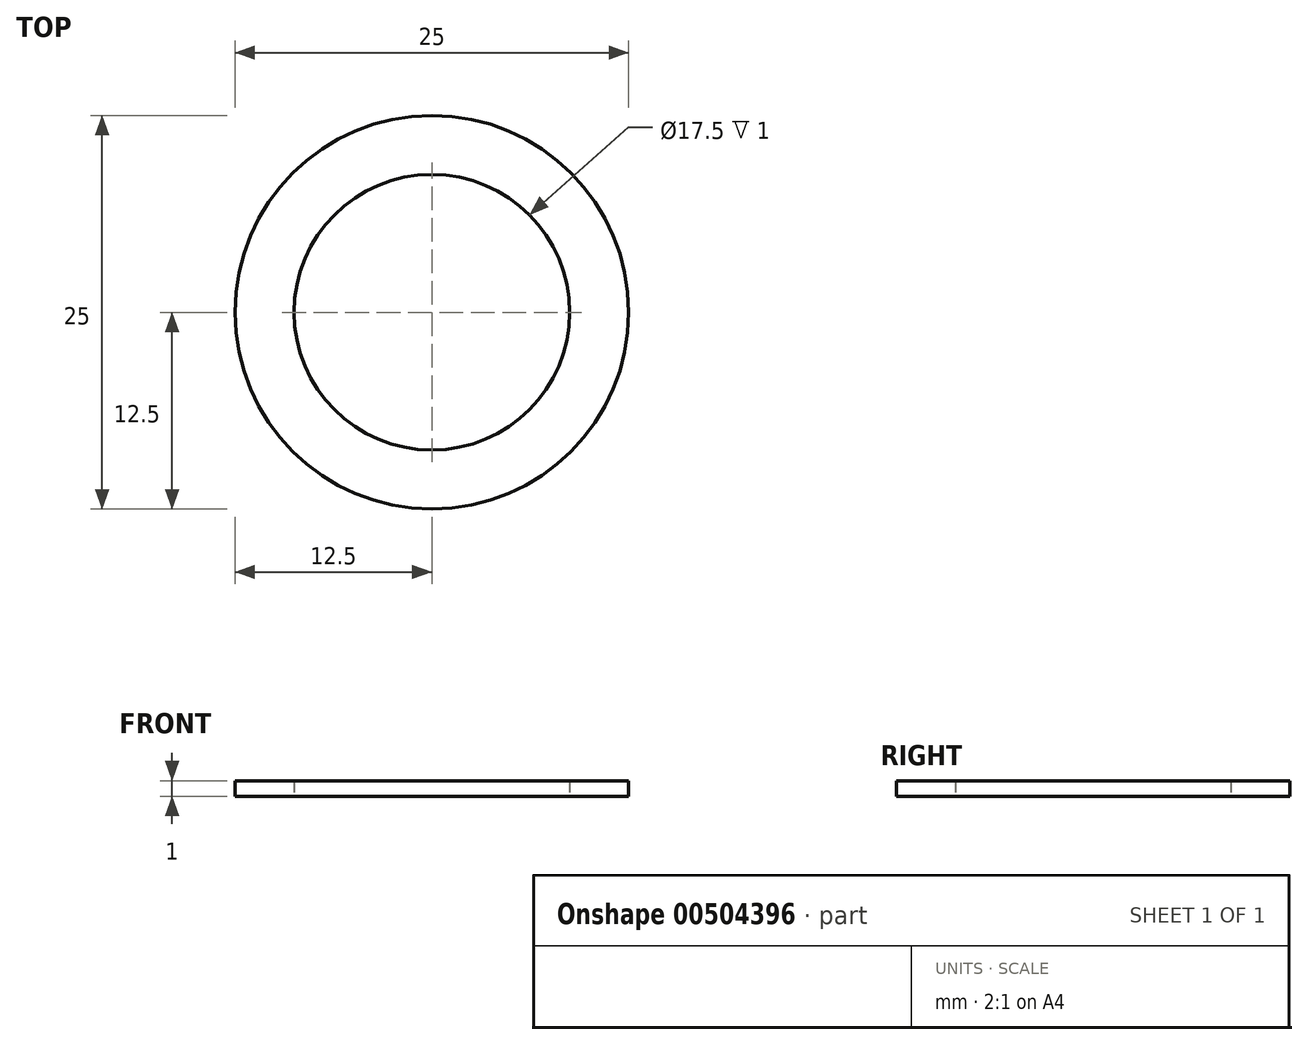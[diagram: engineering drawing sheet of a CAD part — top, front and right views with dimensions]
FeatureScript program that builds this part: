
annotation { "Feature Type Name" : "Feature", "Feature Type Description" : "" }
export const myFeature = defineFeature(function(context is Context, id is Id, definition is map)
    precondition{}
    {
        {
            var Q0;
            Q0=qCreatedBy(makeId("Top.planeOp"),FACE);
            var sketch = newSketch(context, id + "F0", { "sketchPlane" : qUnion([Q0])});
            skCircle(sketch, "E0", {"center": v(0, 0) * mm, "radius": 8.75 * mm});
            skCircle(sketch, "E1", {"center": v(0, 0) * mm, "radius": 12.5 * mm});
            skSolve(sketch);
        }
        {
            var Q0;
            Q0=makeQuery(id+"F0.imprint","IMPRINT",FACE,{"disambiguationData":[TD([[makeQuery(id+"F0.imprint","IMPRINT",EDGE,{"derivedFrom":sQuery(id+"F0.wireOp",EDGE,"E0")}),-1.0]])]});
            extrude(context, id + "F1", {"entities" : qUnion([Q0]), "depth" : 1 * mm});
        }
    });
